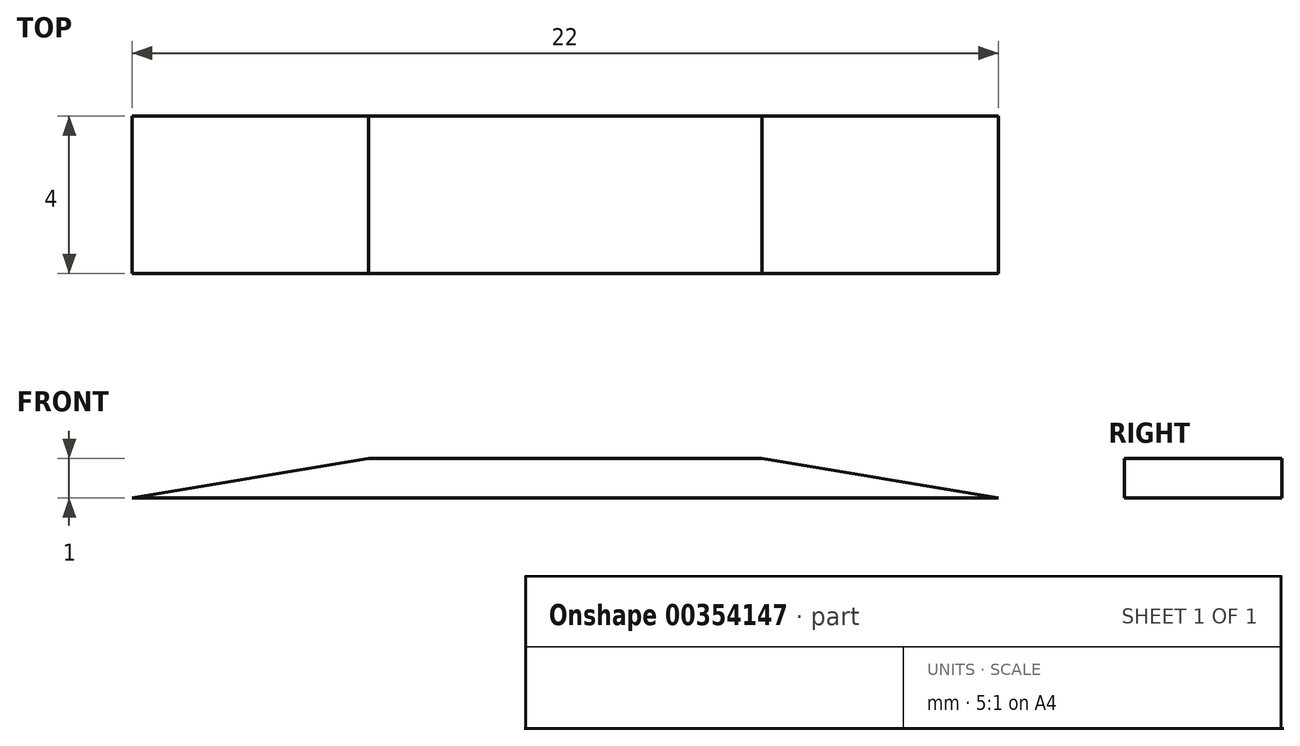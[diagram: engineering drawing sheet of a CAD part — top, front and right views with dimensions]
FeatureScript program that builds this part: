
annotation { "Feature Type Name" : "Feature", "Feature Type Description" : "" }
export const myFeature = defineFeature(function(context is Context, id is Id, definition is map)
    precondition{}
    {
        {
            var Q0;
            Q0=qCreatedBy(makeId("Top.planeOp"),FACE);
            var sketch = newSketch(context, id + "F0", { "sketchPlane" : qUnion([Q0])});
            skLineSegment(sketch, "E0.bottom", {"start": v(0, 0) * mm, "end": v(22, 0) * mm});
            skLineSegment(sketch, "E0.top", {"start": v(0, 4) * mm, "end": v(22, 4) * mm});
            skLineSegment(sketch, "E0.left", {"start": v(0, 0) * mm, "end": v(0, 4) * mm});
            skLineSegment(sketch, "E0.right", {"start": v(22, 0) * mm, "end": v(22, 4) * mm});
            skSolve(sketch);
        }
        {
            var Q0;
            Q0 = qSketchRegion(id + "F0", true);
            extrude(context, id + "F1", {"entities" : qUnion([Q0]), "depth" : 1 * mm});
        }
        {
            var Q0;
            Q0=makeQuery(id+"F1.opExtrude","SWEPT_FACE",FACE,{"disambiguationData":[OSD([sQuery(id+"F0.wireOp",EDGE,"E0.bottom")])]});
            var sketch = newSketch(context, id + "F2", { "sketchPlane" : qUnion([Q0])});
            skLineSegment(sketch, "E1", {"start": v(0, 0) * mm, "end": v(0, 1) * mm});
            skLineSegment(sketch, "E2", {"start": v(0, 1) * mm, "end": v(6, 1) * mm});
            skLineSegment(sketch, "E3", {"start": v(6, 1) * mm, "end": v(0, 0) * mm});
            skLineSegment(sketch, "E4", {"start": v(11, 1) * mm, "end": v(11, 0) * mm, "construction": true});
            skLineSegment(sketch, "E5.MirrorCS", {"start": v(22, 0) * mm, "end": v(22, 1) * mm});
            skLineSegment(sketch, "E6.MirrorCS", {"start": v(22, 1) * mm, "end": v(16, 1) * mm});
            skLineSegment(sketch, "E7.MirrorCS", {"start": v(16, 1) * mm, "end": v(22, 0) * mm});
            skSolve(sketch);
        }
        {
            var Q0;
            Q0=makeQuery(id+"F2.imprint","IMPRINT",FACE,{"disambiguationData":[TD([[makeQuery(id+"F2.imprint","IMPRINT",EDGE,{"derivedFrom":sQuery(id+"F2.wireOp",EDGE,"E1")}),1.0]])]});
            var Q1;
            Q1 = qSketchRegion(id + "F2", true);
            extrude(context, id + "F3", {"entities" : qUnion([Q0, Q1]), "operationType" : NewBodyOperationType.REMOVE, "oppositeDirection" : true, "depth" : 25 * mm});
        }
    });
